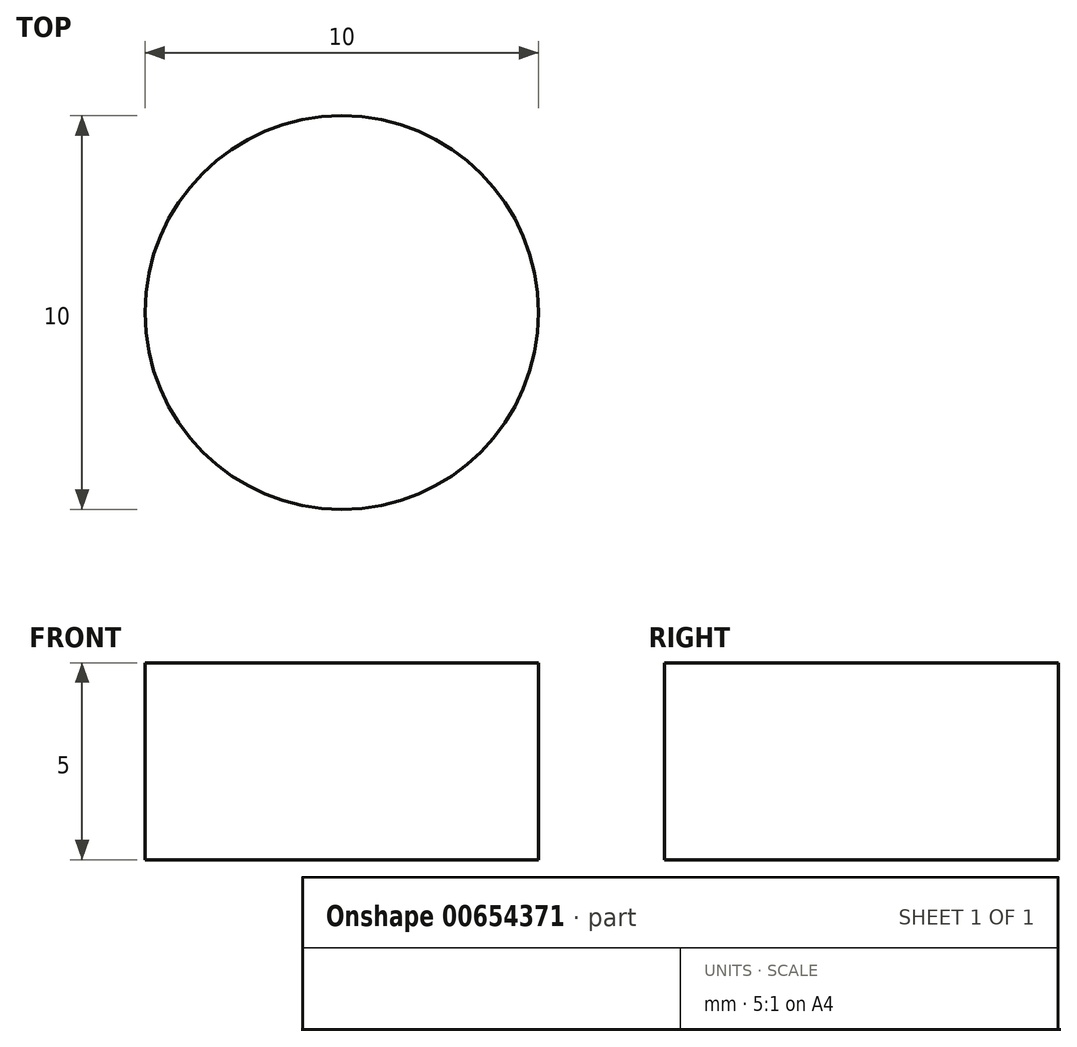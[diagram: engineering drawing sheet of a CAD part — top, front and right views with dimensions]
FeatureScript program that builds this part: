
annotation { "Feature Type Name" : "Feature", "Feature Type Description" : "" }
export const myFeature = defineFeature(function(context is Context, id is Id, definition is map)
    precondition{}
    {
        {
            var Q0;
            Q0=qCreatedBy(makeId("Top.planeOp"),FACE);
            var sketch = newSketch(context, id + "F0", { "sketchPlane" : qUnion([Q0])});
            skCircle(sketch, "E0", {"center": v(0, 0) * mm, "radius": 5 * mm});
            skSolve(sketch);
        }
        {
            var Q0;
            Q0=makeQuery(id+"F0.imprint","IMPRINT",FACE,{"disambiguationData":[TD([[makeQuery(id+"F0.imprint","IMPRINT",EDGE,{"derivedFrom":sQuery(id+"F0.wireOp",EDGE,"E0")}),1.0]])]});
            extrude(context, id + "F1", {"entities" : qUnion([Q0]), "depth" : 5 * mm, "offsetDistance" : 25 * mm});
        }
    });
